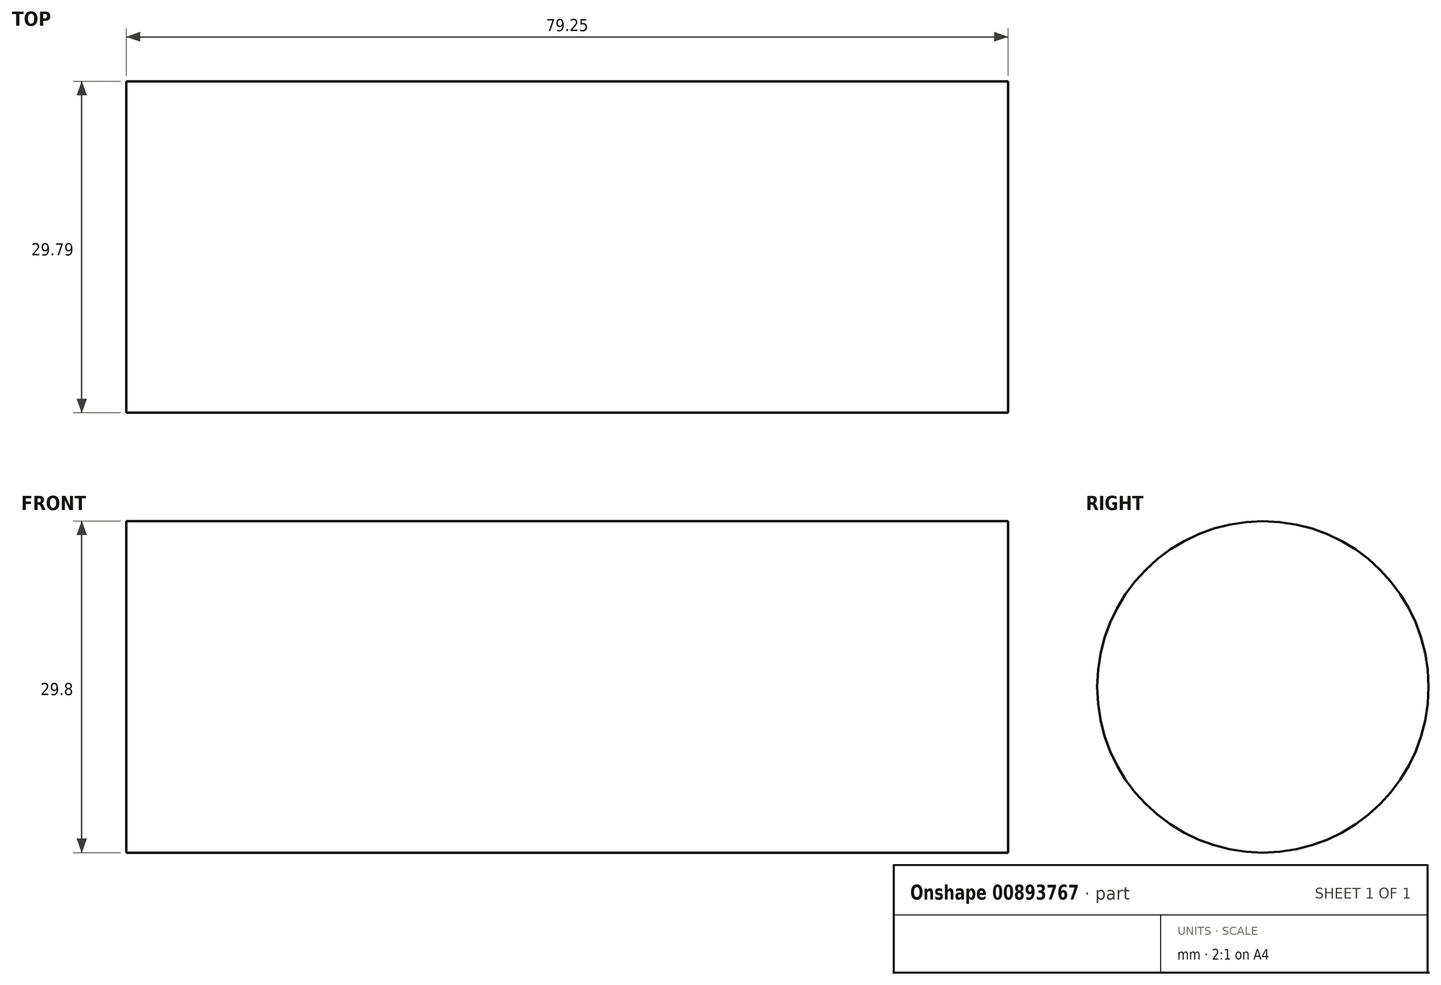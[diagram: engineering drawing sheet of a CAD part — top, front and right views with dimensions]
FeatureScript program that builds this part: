
annotation { "Feature Type Name" : "Feature", "Feature Type Description" : "" }
export const myFeature = defineFeature(function(context is Context, id is Id, definition is map)
    precondition{}
    {
        {
            var Q0;
            Q0=qCreatedBy(makeId("Right.planeOp"),FACE);
            var sketch = newSketch(context, id + "F0", { "sketchPlane" : qUnion([Q0])});
            skCircle(sketch, "E0", {"center": v(-31.1, 20.09) * mm, "radius": 14.9 * mm});
            skSolve(sketch);
        }
        {
            var Q0;
            Q0 = qSketchRegion(id + "F0", true);
            extrude(context, id + "F1", {"entities" : qUnion([Q0]), "depth" : 79.25 * mm, "offsetDistance" : 25.4 * mm});
        }
    });
